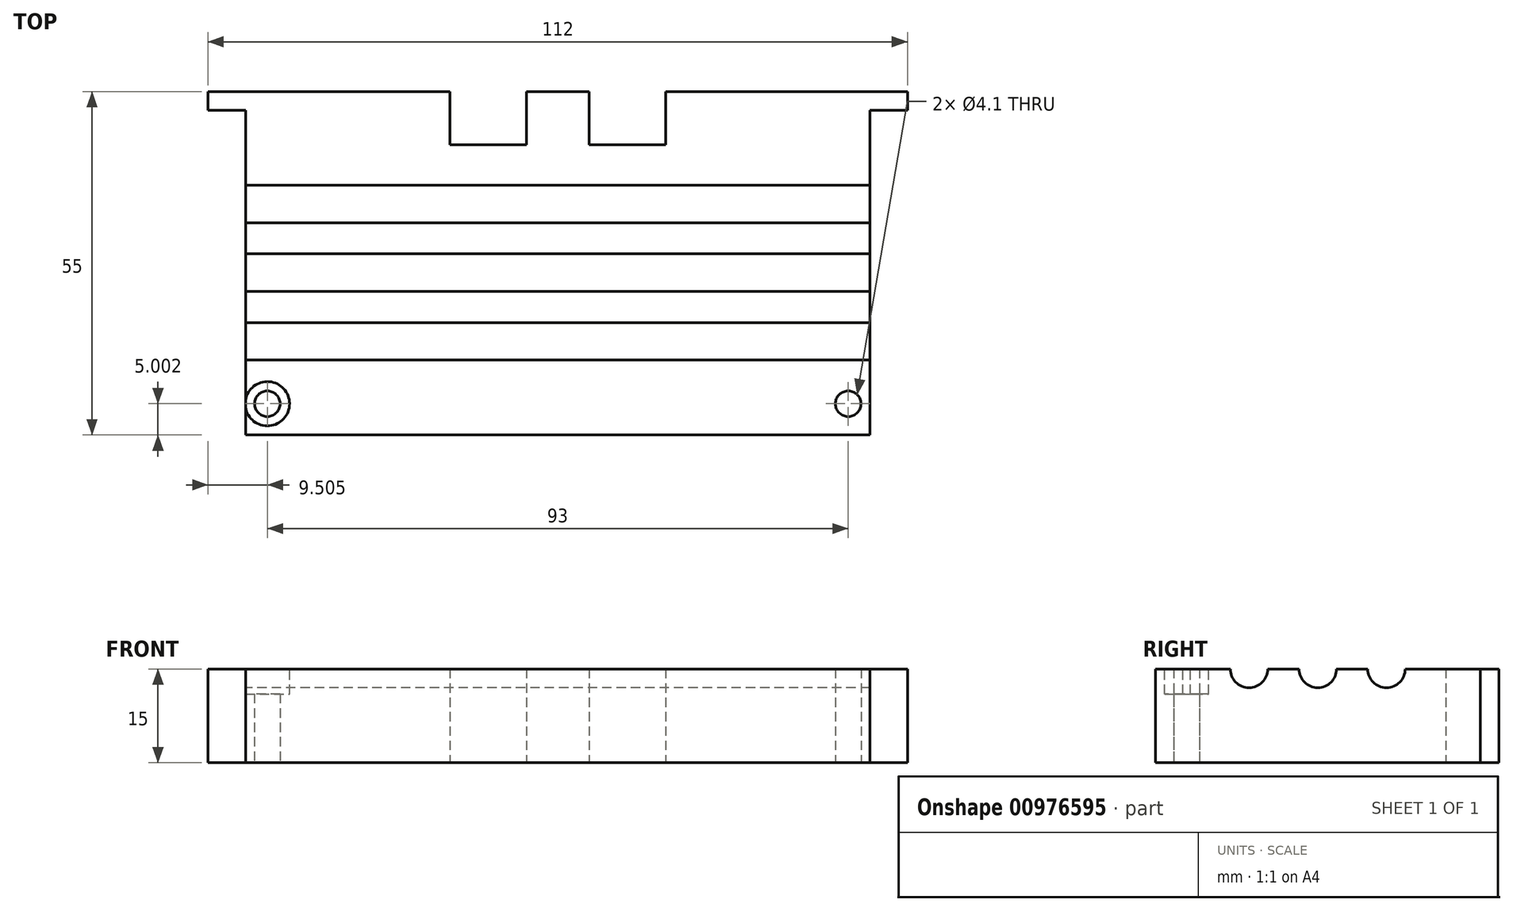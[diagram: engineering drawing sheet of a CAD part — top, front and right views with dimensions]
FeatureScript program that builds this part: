
annotation { "Feature Type Name" : "Feature", "Feature Type Description" : "" }
export const myFeature = defineFeature(function(context is Context, id is Id, definition is map)
    precondition{}
    {
        {
            var Q0;
            Q0=qCreatedBy(makeId("Top.planeOp"),FACE);
            var sketch = newSketch(context, id + "F0", { "sketchPlane" : qUnion([Q0])});
            skLineSegment(sketch, "E0", {"start": v(-82.33, -11.1) * mm, "end": v(-43.63, -11.1) * mm});
            skLineSegment(sketch, "E1", {"start": v(-43.63, -11.1) * mm, "end": v(-43.63, -19.6) * mm});
            skLineSegment(sketch, "E2", {"start": v(-43.63, -19.6) * mm, "end": v(-31.33, -19.6) * mm});
            skLineSegment(sketch, "E3", {"start": v(-31.33, -19.6) * mm, "end": v(-31.33, -11.1) * mm});
            skLineSegment(sketch, "E4", {"start": v(-31.33, -11.1) * mm, "end": v(-21.33, -11.1) * mm});
            skLineSegment(sketch, "E5", {"start": v(-21.33, -11.1) * mm, "end": v(-21.33, -19.6) * mm});
            skLineSegment(sketch, "E6", {"start": v(-21.33, -19.6) * mm, "end": v(-9.03, -19.6) * mm});
            skLineSegment(sketch, "E7", {"start": v(-9.03, -19.6) * mm, "end": v(-9.03, -11.1) * mm});
            skLineSegment(sketch, "E8", {"start": v(-9.03, -11.1) * mm, "end": v(29.67, -11.1) * mm});
            skLineSegment(sketch, "E9", {"start": v(29.67, -11.1) * mm, "end": v(29.67, -14.1) * mm});
            skLineSegment(sketch, "E10", {"start": v(29.67, -14.1) * mm, "end": v(23.67, -14.1) * mm});
            skLineSegment(sketch, "E11", {"start": v(23.67, -14.1) * mm, "end": v(23.67, -66.1) * mm});
            skLineSegment(sketch, "E12", {"start": v(23.67, -66.1) * mm, "end": v(-76.33, -66.1) * mm});
            skLineSegment(sketch, "E13", {"start": v(-76.33, -66.1) * mm, "end": v(-76.33, -14.1) * mm});
            skLineSegment(sketch, "E14", {"start": v(-76.33, -14.1) * mm, "end": v(-82.33, -14.1) * mm});
            skLineSegment(sketch, "E15", {"start": v(-82.33, -14.1) * mm, "end": v(-82.33, -11.1) * mm});
            skCircle(sketch, "E16", {"center": v(-72.83, -61.1) * mm, "radius": 2.05 * mm});
            skCircle(sketch, "E17", {"center": v(20.17, -61.1) * mm, "radius": 2.05 * mm});
            skLineSegment(sketch, "E18", {"start": v(-43.63, -11.1) * mm, "end": v(-42.63, -11.1) * mm});
            skLineSegment(sketch, "E19", {"start": v(-42.63, -11.1) * mm, "end": v(-42.63, -18.6) * mm});
            skLineSegment(sketch, "E20", {"start": v(-42.63, -18.6) * mm, "end": v(-32.33, -18.6) * mm});
            skLineSegment(sketch, "E21", {"start": v(-32.33, -18.6) * mm, "end": v(-32.33, -11.1) * mm});
            skLineSegment(sketch, "E22", {"start": v(-32.33, -11.1) * mm, "end": v(-31.33, -11.1) * mm});
            skLineSegment(sketch, "E23", {"start": v(-21.33, -11.1) * mm, "end": v(-20.33, -11.1) * mm});
            skLineSegment(sketch, "E24", {"start": v(-20.33, -11.1) * mm, "end": v(-20.33, -18.6) * mm});
            skLineSegment(sketch, "E25", {"start": v(-20.33, -18.6) * mm, "end": v(-10.03, -18.6) * mm});
            skLineSegment(sketch, "E26", {"start": v(-10.03, -18.6) * mm, "end": v(-10.03, -11.1) * mm});
            skLineSegment(sketch, "E27", {"start": v(-10.03, -11.1) * mm, "end": v(-9.03, -11.1) * mm});
            skSolve(sketch);
        }
        {
            var Q0;
            Q0=makeQuery(id+"F0.imprint","IMPRINT",FACE,{"disambiguationData":[TD([[makeQuery(id+"F0.imprint","IMPRINT",EDGE,{"derivedFrom":sQuery(id+"F0.wireOp",EDGE,"E0")}),-1.0]])]});
            extrude(context, id + "F1", {"entities" : qUnion([Q0]), "depth" : 15 * mm, "offsetDistance" : 25 * mm});
        }
        {
            var Q0;
            Q0=makeQuery(id+"F1.opExtrude","SWEPT_FACE",FACE,{"disambiguationData":[OSD([sQuery(id+"F0.wireOp",EDGE,"E13")])]});
            var sketch = newSketch(context, id + "F2", { "sketchPlane" : qUnion([Q0])});
            skCircle(sketch, "E28", {"center": v(29.1, 15) * mm, "radius": 3 * mm});
            skCircle(sketch, "E29", {"center": v(51.1, 15) * mm, "radius": 3 * mm});
            skCircle(sketch, "E30", {"center": v(40.1, 15) * mm, "radius": 3 * mm});
            skSolve(sketch);
        }
        {
            var Q0;
            Q0 = qSketchRegion(id + "F2", true);
            extrude(context, id + "F3", {"entities" : qUnion([Q0]), "operationType" : NewBodyOperationType.REMOVE, "oppositeDirection" : true, "depth" : 121 * mm, "offsetDistance" : 25 * mm});
        }
        {
            var Q0;
            {var subQ0=sQuery(id+"F0.wireOp",EDGE,"E13");var subQ1=sQuery(id+"F0.wireOp",EDGE,"E12");var subQ2=sQuery(id+"F0.wireOp",EDGE,"E16");var subQ3=sQuery(id+"F0.wireOp",EDGE,"E11");var subQ4=sQuery(id+"F0.wireOp",EDGE,"E17");Q0=makeQuery(id+"F3.boolean.opBoolean","SPLIT",FACE,{"disambiguationData":[TD([makeQuery(id+"F1.opExtrude","SWEPT_FACE",FACE,{"disambiguationData":[OSD([subQ3])]}),makeQuery(id+"F1.opExtrude","SWEPT_FACE",FACE,{"disambiguationData":[OSD([subQ1])]}),makeQuery(id+"F1.opExtrude","SWEPT_FACE",FACE,{"disambiguationData":[OSD([subQ0])]}),makeQuery(id+"F1.opExtrude","SWEPT_FACE",FACE,{"disambiguationData":[OSD([subQ2])]}),makeQuery(id+"F1.opExtrude","SWEPT_FACE",FACE,{"disambiguationData":[OSD([subQ4])]}),makeQuery(id+"F3.opExtrude","SWEPT_FACE",FACE,{"disambiguationData":[OSD([sQuery(id+"F2.wireOp",EDGE,"E29")])]})])],"derivedFrom":makeQuery(id+"F1.opExtrude","CAP_FACE",FACE,{"disambiguationData":[OSD([sQuery(id+"F0.wireOp",EDGE,"E0"),sQuery(id+"F0.wireOp",EDGE,"E1"),sQuery(id+"F0.wireOp",EDGE,"E2"),sQuery(id+"F0.wireOp",EDGE,"E3"),sQuery(id+"F0.wireOp",EDGE,"E4"),sQuery(id+"F0.wireOp",EDGE,"E5"),sQuery(id+"F0.wireOp",EDGE,"E6"),sQuery(id+"F0.wireOp",EDGE,"E7"),sQuery(id+"F0.wireOp",EDGE,"E8"),sQuery(id+"F0.wireOp",EDGE,"E9"),sQuery(id+"F0.wireOp",EDGE,"E10"),subQ3,subQ1,subQ0,sQuery(id+"F0.wireOp",EDGE,"E14"),sQuery(id+"F0.wireOp",EDGE,"E15"),subQ2,subQ4])],"isStart":false})});}
            var sketch = newSketch(context, id + "F4", { "sketchPlane" : qUnion([Q0])});
            skCircle(sketch, "E31", {"center": v(-72.83, -61.1) * mm, "radius": 3.55 * mm});
            skCircle(sketch, "E32", {"center": v(20.17, -61.1) * mm, "radius": 3.55 * mm});
            skSolve(sketch);
        }
        {
            var Q0;
            {var subQ1=sQuery(id+"F0.wireOp",EDGE,"E16");Q0=makeQuery(id+"F4.imprint","IMPRINT",FACE,{"disambiguationData":[TD([[makeQuery(id+"F4.imprint","IMPRINT",EDGE,{"derivedFrom":makeQuery(id+"F1.opExtrude","CAP_EDGE",EDGE,{"disambiguationData":[OSD([subQ1])],"isStart":false})}),-1.0]])]});}
            extrude(context, id + "F5", {"entities" : qUnion([Q0]), "operationType" : NewBodyOperationType.REMOVE, "oppositeDirection" : true, "depth" : 4 * mm, "offsetDistance" : 25 * mm});
        }
    });
